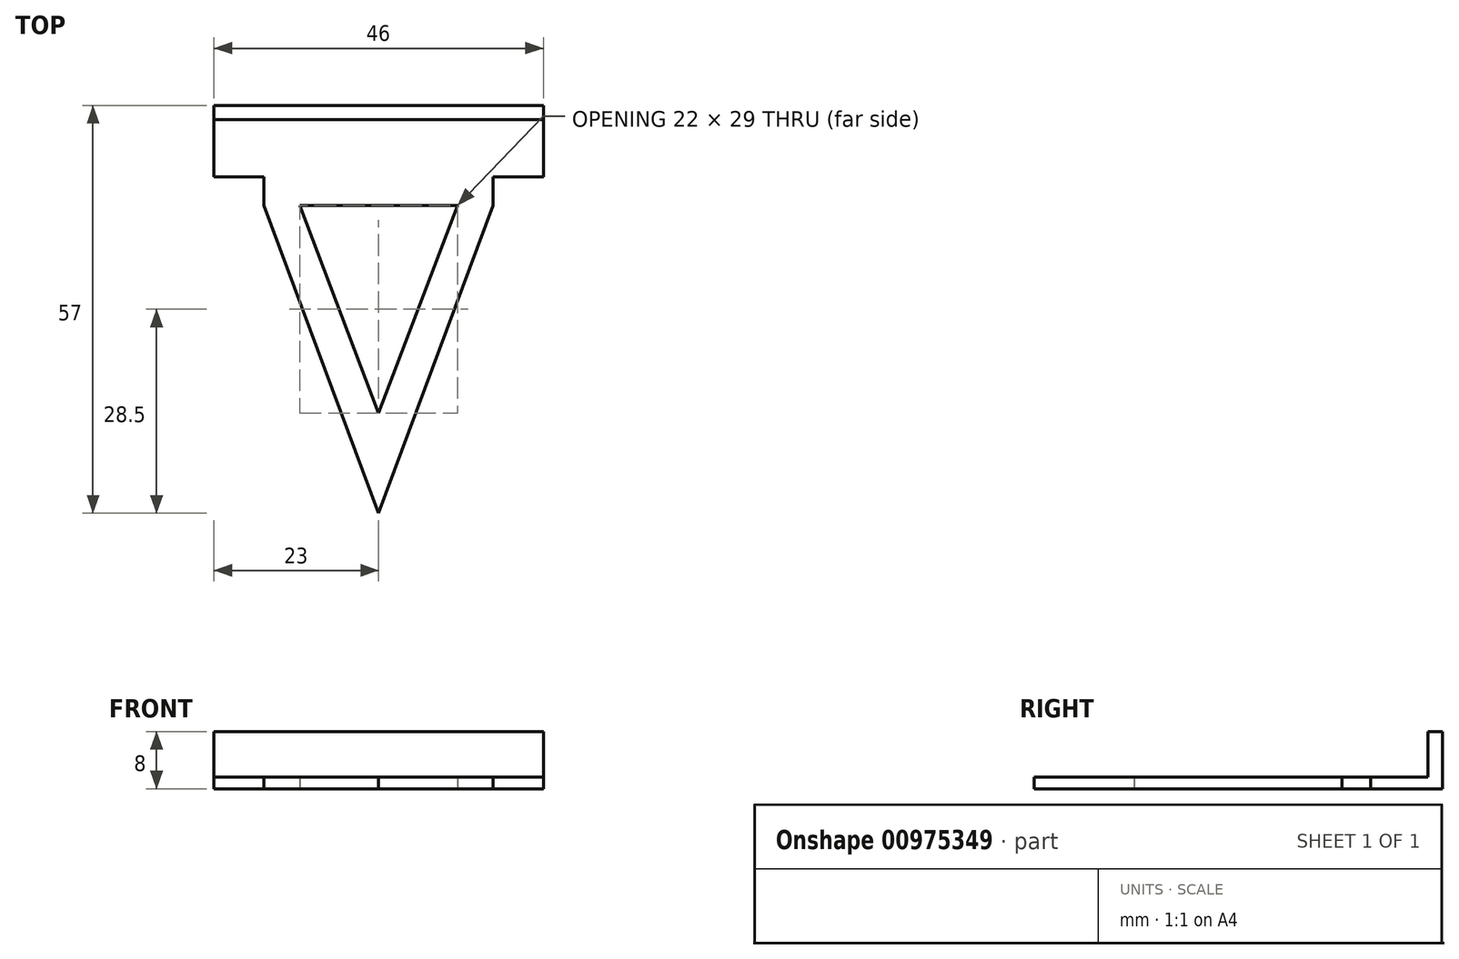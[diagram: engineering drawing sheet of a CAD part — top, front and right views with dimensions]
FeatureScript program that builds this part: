
annotation { "Feature Type Name" : "Feature", "Feature Type Description" : "" }
export const myFeature = defineFeature(function(context is Context, id is Id, definition is map)
    precondition{}
    {
        {
            var Q0;
            Q0=qCreatedBy(makeId("Top.planeOp"),FACE);
            var sketch = newSketch(context, id + "F0", { "sketchPlane" : qUnion([Q0])});
            skLineSegment(sketch, "E0.bottom", {"start": v(0, 0) * mm, "end": v(46, 0) * mm});
            skLineSegment(sketch, "E0.top", {"start": v(0, 10) * mm, "end": v(46, 10) * mm});
            skLineSegment(sketch, "E0.left", {"start": v(0, 0) * mm, "end": v(0, 10) * mm});
            skLineSegment(sketch, "E0.right", {"start": v(46, 0) * mm, "end": v(46, 10) * mm});
            skLineSegment(sketch, "E1.bottom", {"start": v(7, 0) * mm, "end": v(39, 0) * mm, "construction": true});
            skLineSegment(sketch, "E1.top", {"start": v(7, -4) * mm, "end": v(39, -4) * mm, "construction": true});
            skLineSegment(sketch, "E1.left", {"start": v(7, 0) * mm, "end": v(7, -4) * mm});
            skLineSegment(sketch, "E1.right", {"start": v(39, 0) * mm, "end": v(39, -4) * mm});
            skPoint(sketch, "E2", {"position": v(23, 10) * mm});
            skPoint(sketch, "E3", {"position": v(23, -47) * mm});
            skLineSegment(sketch, "E4", {"start": v(7, -4) * mm, "end": v(23, -47) * mm});
            skLineSegment(sketch, "E5", {"start": v(39, -4) * mm, "end": v(23, -47) * mm});
            skPoint(sketch, "E6", {"position": v(12, -4) * mm});
            skPoint(sketch, "E7", {"position": v(34, -4) * mm});
            skPoint(sketch, "E8", {"position": v(23, -33) * mm});
            skLineSegment(sketch, "E9", {"start": v(12, -4) * mm, "end": v(23, -33) * mm});
            skLineSegment(sketch, "E10", {"start": v(34, -4) * mm, "end": v(23, -33) * mm});
            skLineSegment(sketch, "E11", {"start": v(12, -4) * mm, "end": v(34, -4) * mm});
            skSolve(sketch);
        }
        {
            var Q0;
            Q0 = qSketchRegion(id + "F0", true);
            extrude(context, id + "F1", {"entities" : qUnion([Q0]), "depth" : 1.6 * mm, "offsetDistance" : 25 * mm});
        }
        {
            var Q0;
            Q0=makeQuery(id+"F1.opExtrude","CAP_FACE",FACE,{"disambiguationData":[OSD([sQuery(id+"F0.wireOp",EDGE,"E0.bottom"),sQuery(id+"F0.wireOp",EDGE,"E0.top"),sQuery(id+"F0.wireOp",EDGE,"E0.left"),sQuery(id+"F0.wireOp",EDGE,"E0.right"),sQuery(id+"F0.wireOp",EDGE,"E1.left"),sQuery(id+"F0.wireOp",EDGE,"E1.right"),sQuery(id+"F0.wireOp",EDGE,"E4"),sQuery(id+"F0.wireOp",EDGE,"E5"),sQuery(id+"F0.wireOp",EDGE,"E9"),sQuery(id+"F0.wireOp",EDGE,"E10"),sQuery(id+"F0.wireOp",EDGE,"E11")])],"isStart":false});
            var sketch = newSketch(context, id + "F2", { "sketchPlane" : qUnion([Q0])});
            skLineSegment(sketch, "E12.bottom", {"start": v(0, 10) * mm, "end": v(46, 10) * mm});
            skLineSegment(sketch, "E12.top", {"start": v(0, 8) * mm, "end": v(46, 8) * mm});
            skLineSegment(sketch, "E12.left", {"start": v(0, 10) * mm, "end": v(0, 8) * mm});
            skLineSegment(sketch, "E12.right", {"start": v(46, 10) * mm, "end": v(46, 8) * mm});
            skSolve(sketch);
        }
        {
            var Q0;
            Q0 = qSketchRegion(id + "F2", true);
            extrude(context, id + "F3", {"entities" : qUnion([Q0]), "operationType" : NewBodyOperationType.ADD, "depth" : (8 - 1.6) * mm, "offsetDistance" : 25 * mm});
        }
    });
